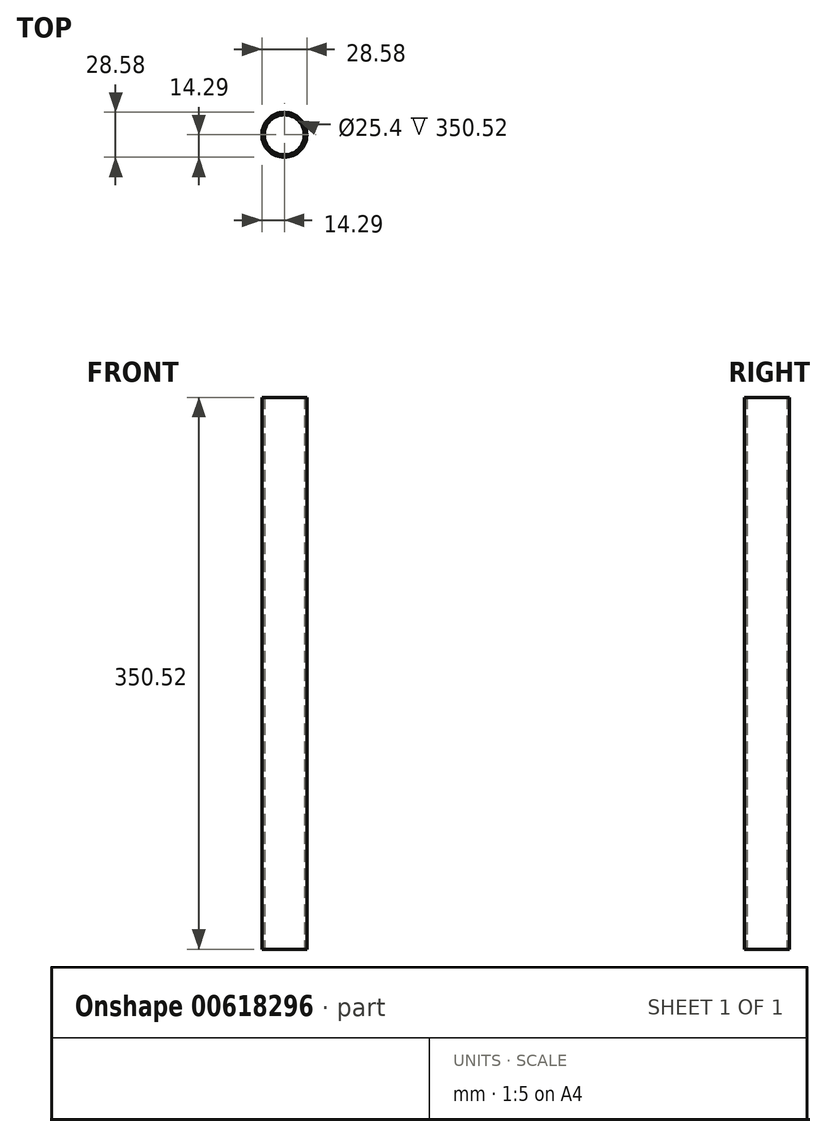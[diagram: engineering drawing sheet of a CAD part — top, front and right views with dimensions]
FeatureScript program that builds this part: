
annotation { "Feature Type Name" : "Feature", "Feature Type Description" : "" }
export const myFeature = defineFeature(function(context is Context, id is Id, definition is map)
    precondition{}
    {
        {
            var Q0;
            Q0=qCreatedBy(makeId("Top.planeOp"),FACE);
            var sketch = newSketch(context, id + "F0", { "sketchPlane" : qUnion([Q0])});
            skLineSegment(sketch, "E0", {"start": v(0, 0) * mm, "end": v(12.7, 0) * mm});
            skCircle(sketch, "E1", {"center": v(0, 0) * mm, "radius": 12.7 * mm});
            skCircle(sketch, "E2.0", {"center": v(0, 0) * mm, "radius": 14.29 * mm});
            skSolve(sketch);
        }
        {
            var Q0;
            Q0=qCreatedBy(makeId("Top.planeOp"),FACE);
            var sketch = newSketch(context, id + "F1", { "sketchPlane" : qUnion([Q0])});
            skSolve(sketch);
        }
        {
            var Q0;
            Q0=qSketchRegion(id+"F1",true);
            var Q1;
            Q1=makeQuery(id+"F0.imprint","IMPRINT",FACE,{"disambiguationData":[TD([[makeQuery(id+"F0.imprint","IMPRINT",EDGE,{"derivedFrom":sQuery(id+"F0.wireOp",EDGE,"E1")}),-1.0]])]});
            extrude(context, id + "F2", {"entities" : qUnion([Q0, Q1]), "depth" : 350.52 * mm, "offsetDistance" : 25.4 * mm});
        }
    });
